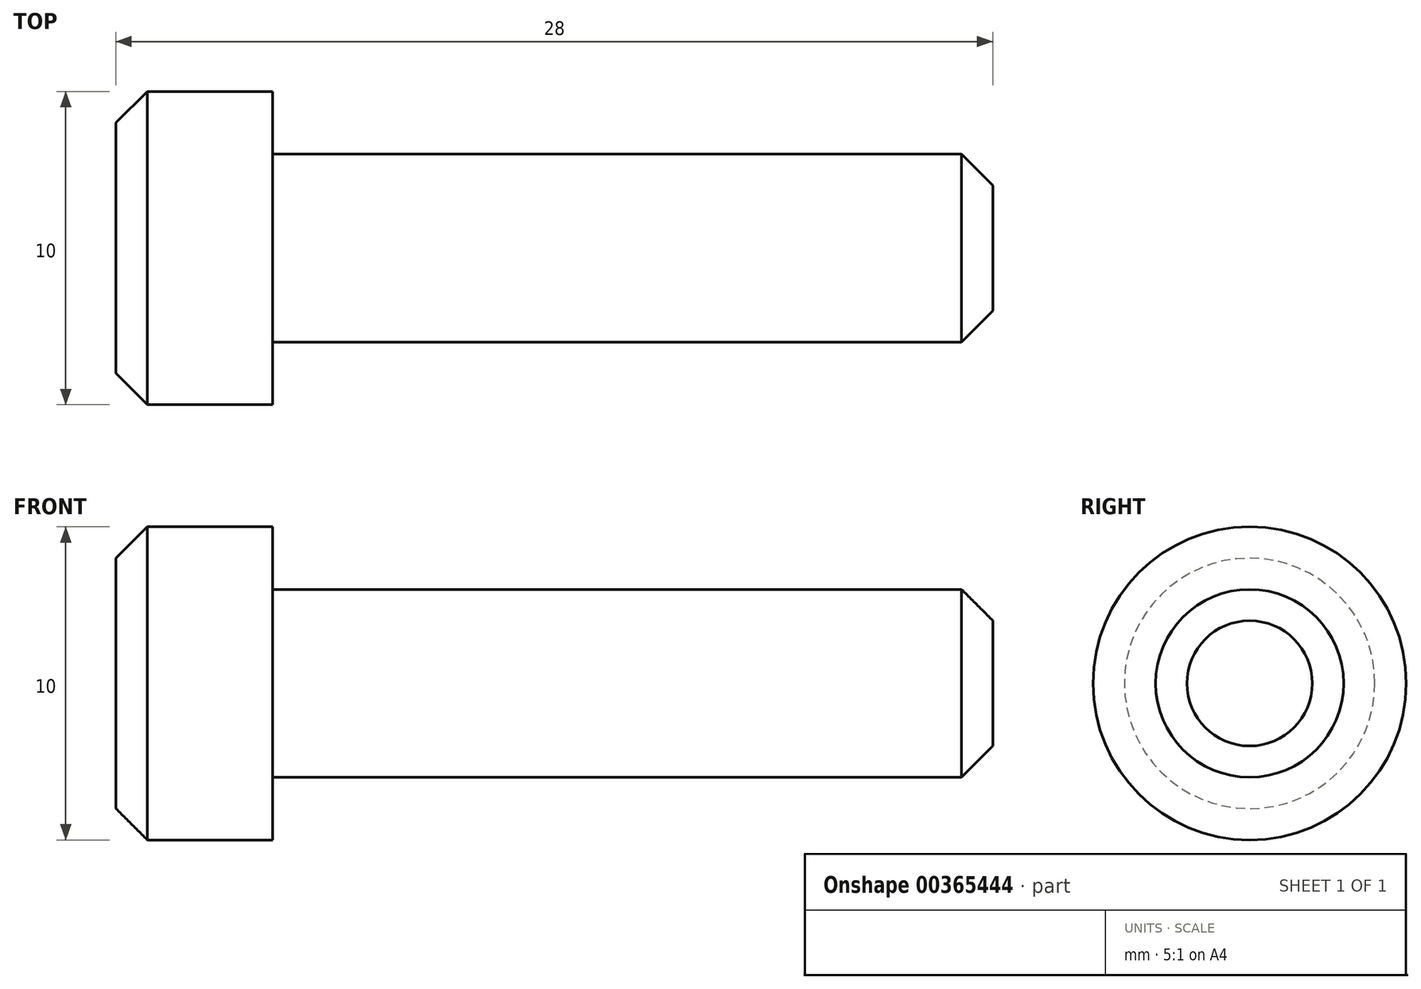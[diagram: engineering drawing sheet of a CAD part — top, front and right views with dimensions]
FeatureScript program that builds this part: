
annotation { "Feature Type Name" : "Feature", "Feature Type Description" : "" }
export const myFeature = defineFeature(function(context is Context, id is Id, definition is map)
    precondition{}
    {
        {
            var Q0;
            Q0=qCreatedBy(makeId("Front.planeOp"),FACE);
            var sketch = newSketch(context, id + "F0", { "sketchPlane" : qUnion([Q0])});
            skLineSegment(sketch, "E0", {"start": v(5.37, 0) * mm, "end": v(5.37, 3) * mm});
            skLineSegment(sketch, "E1", {"start": v(5.37, 3) * mm, "end": v(-17.63, 3) * mm});
            skLineSegment(sketch, "E2", {"start": v(-17.63, 3) * mm, "end": v(-17.63, 5) * mm});
            skLineSegment(sketch, "E3", {"start": v(-17.63, 5) * mm, "end": v(-22.63, 5) * mm});
            skLineSegment(sketch, "E4", {"start": v(-22.63, 5) * mm, "end": v(-22.63, 0) * mm});
            skLineSegment(sketch, "E5", {"start": v(-22.63, 0) * mm, "end": v(5.37, 0) * mm});
            skSolve(sketch);
        }
        {
            var Q0;
            Q0 = qSketchRegion(id + "F0", true);
            var Q1;
            Q1=sQuery(id+"F0.wireOp",EDGE,"E5");
            revolve(context, id + "F1", {"entities" : qUnion([Q0]), "axis" : qUnion([Q1]), "revolveType" : RevolveType.FULL});
        }
        {
            var Q0;
            Q0=makeQuery(id+"F1.opRevolve","SWEPT_EDGE",EDGE,{"disambiguationData":[OSD([sQuery(id+"F0.wireOp",EDGE,"E0"),sQuery(id+"F0.wireOp",EDGE,"E1")])]});
            var Q1;
            Q1=makeQuery(id+"F1.opRevolve","SWEPT_EDGE",EDGE,{"disambiguationData":[OSD([sQuery(id+"F0.wireOp",EDGE,"E3"),sQuery(id+"F0.wireOp",EDGE,"E4")])]});
            chamfer(context, id + "F2", {"entities" : qUnion([Q0, Q1]), "width" : 1 * mm, "tangentPropagation" : true});
        }
    });
